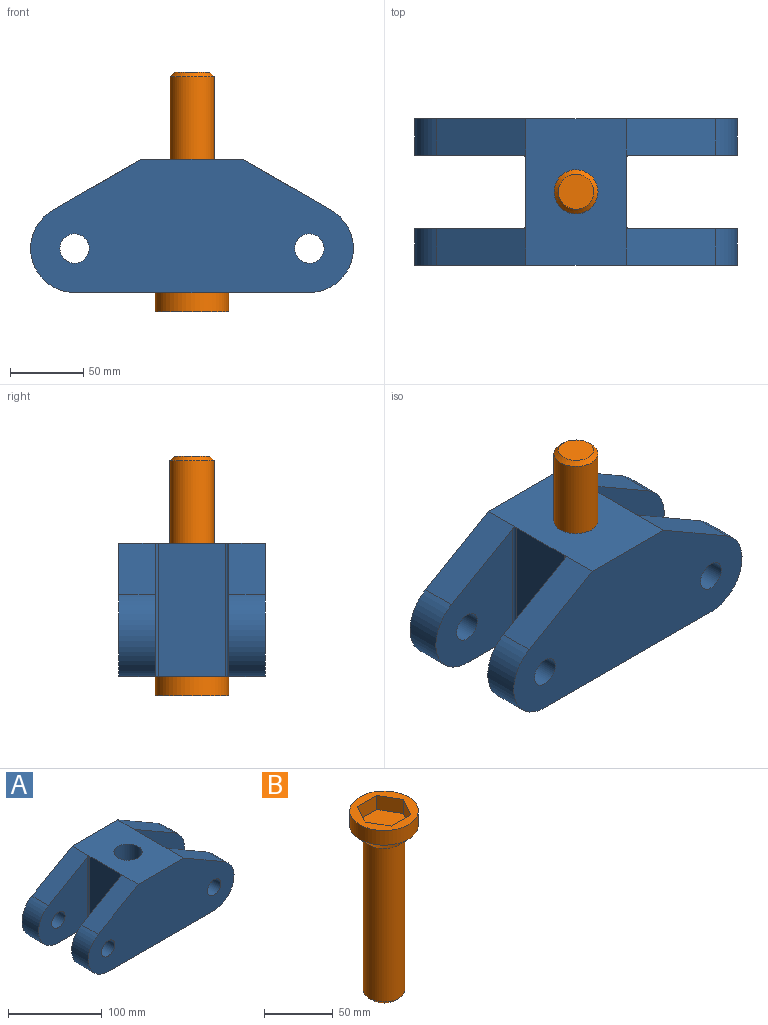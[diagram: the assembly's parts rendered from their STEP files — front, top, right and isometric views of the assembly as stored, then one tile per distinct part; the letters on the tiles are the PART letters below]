
ASSEMBLY  parts=2 mates=1
PART A: 28 faces, bbox 220x100x91 mm
  f0: cylinder r=30mm len=55.98mm, axis (0,1,0), area 1963.5mm2, adj f1,f5,f8,f11
  f1: plane 160x100mm, normal (0,0,-1), area 9477.8mm2, adj f0,f2,f8,f9,f10,f11,f12,f13
  f2: cylinder r=30mm len=55.98mm, axis (0,1,0), area 1963.5mm2, adj f1,f3,f8,f9
  f3: plane 60.62x35mm, normal (0.5,0,0.87), area 1751mm2, adj f2,f7,f8,f9,f27
  f4: cylinder r=10mm len=25mm, axis (0,1,0), area 1570.8mm2, adj f8,f11
  f5: plane 60.62x35mm, normal (-0.5,0,0.87), area 1751mm2, adj f0,f7,f8,f11,f26
  f6: cylinder r=10mm len=25mm, axis (0,1,0), area 1570.8mm2, adj f8,f9
  f7: plane 100x68.76mm, normal (0,0,1), area 6168.8mm2, adj f3,f5,f8,f10,f12,f15,f17,f19
  f8: plane 220x90.98mm, normal (0,-1,0), area 15602.7mm2, adj f0,f1,f2,f3,f4,f5,f6,f7
  f9: plane 89.83x73.62mm, normal (0,1,0), area 4492.8mm2, adj f1,f2,f3,f6,f27
  f10: plane 90.98x46mm, normal (1,0,0), area 4185.1mm2, adj f1,f7,f24,f27
  f11: plane 89.83x73.62mm, normal (0,1,0), area 4492.8mm2, adj f0,f1,f4,f5,f26
  f12: plane 90.98x46mm, normal (-1,0,0), area 4185.1mm2, adj f1,f7,f25,f26
  f13: cylinder r=30mm len=55.98mm, axis (0,-1,0), area 1963.5mm2, adj f1,f17,f19,f21
  f14: cylinder r=30mm len=55.98mm, axis (0,-1,0), area 1963.5mm2, adj f1,f15,f19,f20
  f15: plane 60.62x35mm, normal (0.5,0,0.87), area 1751mm2, adj f7,f14,f19,f20,f24
  f16: cylinder r=10mm len=25mm, axis (0,-1,0), area 1570.8mm2, adj f19,f21
  f17: plane 60.62x35mm, normal (-0.5,0,0.87), area 1751mm2, adj f7,f13,f19,f21,f25
  f18: cylinder r=10mm len=25mm, axis (0,-1,0), area 1570.8mm2, adj f19,f20
  f19: plane 220x90.98mm, normal (0,1,0), area 15602.7mm2, adj f1,f7,f13,f14,f15,f16,f17,f18
  f20: plane 89.83x73.62mm, normal (0,-1,0), area 4492.8mm2, adj f1,f14,f15,f18,f24
  f21: plane 89.83x73.62mm, normal (0,-1,0), area 4492.8mm2, adj f1,f13,f16,f17,f25
  f22: cylinder r=15mm len=80.98mm, axis (0,0,1), area 7632.3mm2, adj f7,f23
  f23: cone r=15mm half-angle=45deg, axis (0,0,-1), area 1777.2mm2, adj f1,f22
  f24: cylinder r=2mm len=90.98mm, axis (0,0,-1), area 284.5mm2, adj f1,f10,f15,f20
  f25: cylinder r=2mm len=90.98mm, axis (0,0,1), area 284.5mm2, adj f1,f12,f17,f21
  f26: cylinder r=2mm len=90.98mm, axis (0,0,1), area 284.5mm2, adj f1,f5,f11,f12
  f27: cylinder r=2mm len=90.98mm, axis (0,0,-1), area 284.5mm2, adj f1,f3,f9,f10
PART B: 13 faces, bbox 50x50x163 mm
  f0: plane 50x50mm, normal (0,0,1), area 924.3mm2, adj f4,f5,f6,f7,f8,f9,f10
  f1: plane 24x24mm, normal (0,0,-1), area 452.4mm2, adj f12
  f2: cylinder r=15mm len=137mm, axis (0,0,1), area 12911.9mm2, adj f3,f12
  f3: cone r=15mm half-angle=45deg, axis (0,0,1), area 1777.2mm2, adj f2,f4
  f4: cylinder r=25mm len=50mm, axis (0,0,1), area 2042mm2, adj f0,f3
  f5: plane 20x12.5mm, normal (0,1,0), area 250mm2, adj f0,f6,f10,f11
  f6: plane 17.32x12.5mm, normal (-0.87,0.5,0), area 250mm2, adj f0,f5,f7,f11
  f7: plane 17.32x12.5mm, normal (-0.87,-0.5,0), area 250mm2, adj f0,f6,f8,f11
  f8: plane 20x12.5mm, normal (0,-1,0), area 250mm2, adj f0,f7,f9,f11
  f9: plane 17.32x12.5mm, normal (0.87,-0.5,0), area 250mm2, adj f0,f8,f10,f11
  f10: plane 17.32x12.5mm, normal (0.87,0.5,0), area 250mm2, adj f0,f5,f9,f11
  f11: plane 40x34.64mm, normal (0,0,1), area 1039.2mm2, adj f5,f6,f7,f8,f9,f10
  f12: cone r=15mm half-angle=45deg, axis (0,0,1), area 359.9mm2, adj f1,f2
PLACE A t=(0,0,-50.49)mm
PLACE B rot(axis=(1,0,0),180deg) t=(0,0,99.51)mm
MATE cylindrical B.f2 <-> A.f22  axis (0,0,-1) through (0,0,-40.49)mm
